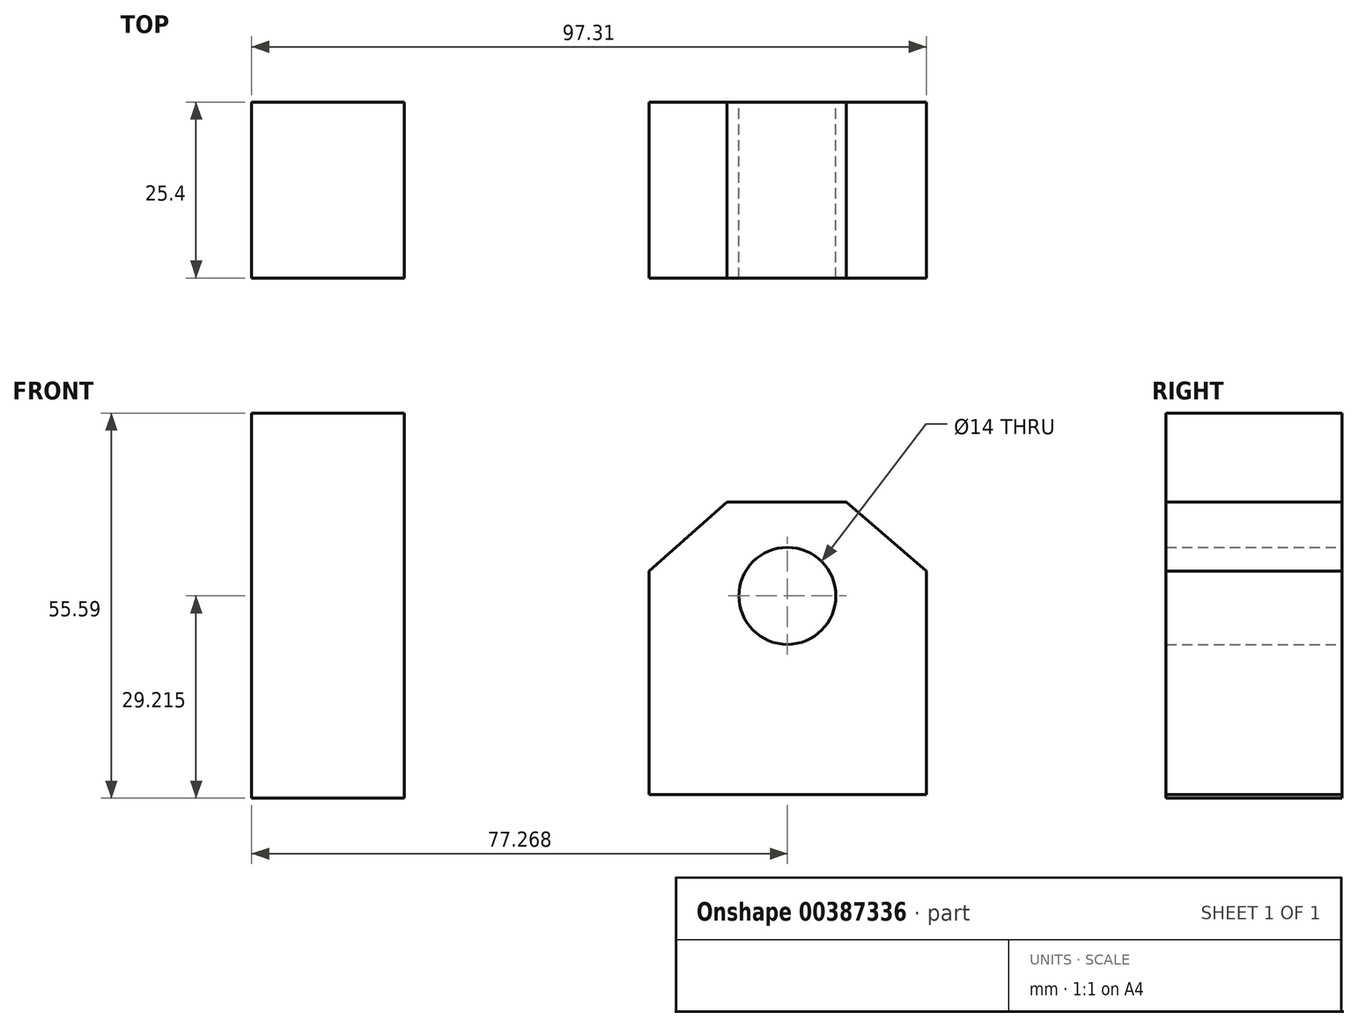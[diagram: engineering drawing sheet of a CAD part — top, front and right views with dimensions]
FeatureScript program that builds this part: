
annotation { "Feature Type Name" : "Feature", "Feature Type Description" : "" }
export const myFeature = defineFeature(function(context is Context, id is Id, definition is map)
    precondition{}
    {
        {
            var Q0;
            Q0=qCreatedBy(makeId("Front.planeOp"),FACE);
            var sketch = newSketch(context, id + "F0", { "sketchPlane" : qUnion([Q0])});
            skLineSegment(sketch, "E0.bottom", {"start": v(-51.94, 36.25) * mm, "end": v(-29.95, 36.25) * mm});
            skLineSegment(sketch, "E0.top", {"start": v(-51.94, -19.34) * mm, "end": v(-29.95, -19.34) * mm});
            skLineSegment(sketch, "E0.left", {"start": v(-51.94, 36.25) * mm, "end": v(-51.94, -19.34) * mm});
            skLineSegment(sketch, "E0.right", {"start": v(-29.95, 36.25) * mm, "end": v(-29.95, -19.34) * mm});
            skLineSegment(sketch, "E1", {"start": v(-51.94, 24.97) * mm, "end": v(-29.95, 24.97) * mm});
            skLineSegment(sketch, "E2.top", {"start": v(5.37, -18.8) * mm, "end": v(45.37, -18.8) * mm});
            skLineSegment(sketch, "E2.left", {"start": v(5.37, 13.42) * mm, "end": v(5.37, -18.8) * mm});
            skLineSegment(sketch, "E2.right", {"start": v(45.37, 13.42) * mm, "end": v(45.37, -18.8) * mm});
            skLineSegment(sketch, "E3", {"start": v(5.37, 13.42) * mm, "end": v(16.65, 23.43) * mm});
            skLineSegment(sketch, "E4", {"start": v(16.65, 23.43) * mm, "end": v(33.83, 23.43) * mm});
            skLineSegment(sketch, "E5", {"start": v(33.83, 23.43) * mm, "end": v(45.37, 13.42) * mm});
            skCircle(sketch, "E6", {"center": v(25.33, 9.88) * mm, "radius": 7 * mm});
            skSolve(sketch);
        }
        {
            var Q0;
            Q0 = qSketchRegion(id + "F0", true);
            extrude(context, id + "F1", {"entities" : qUnion([Q0]), "depth" : 25.4 * mm});
        }
    });
